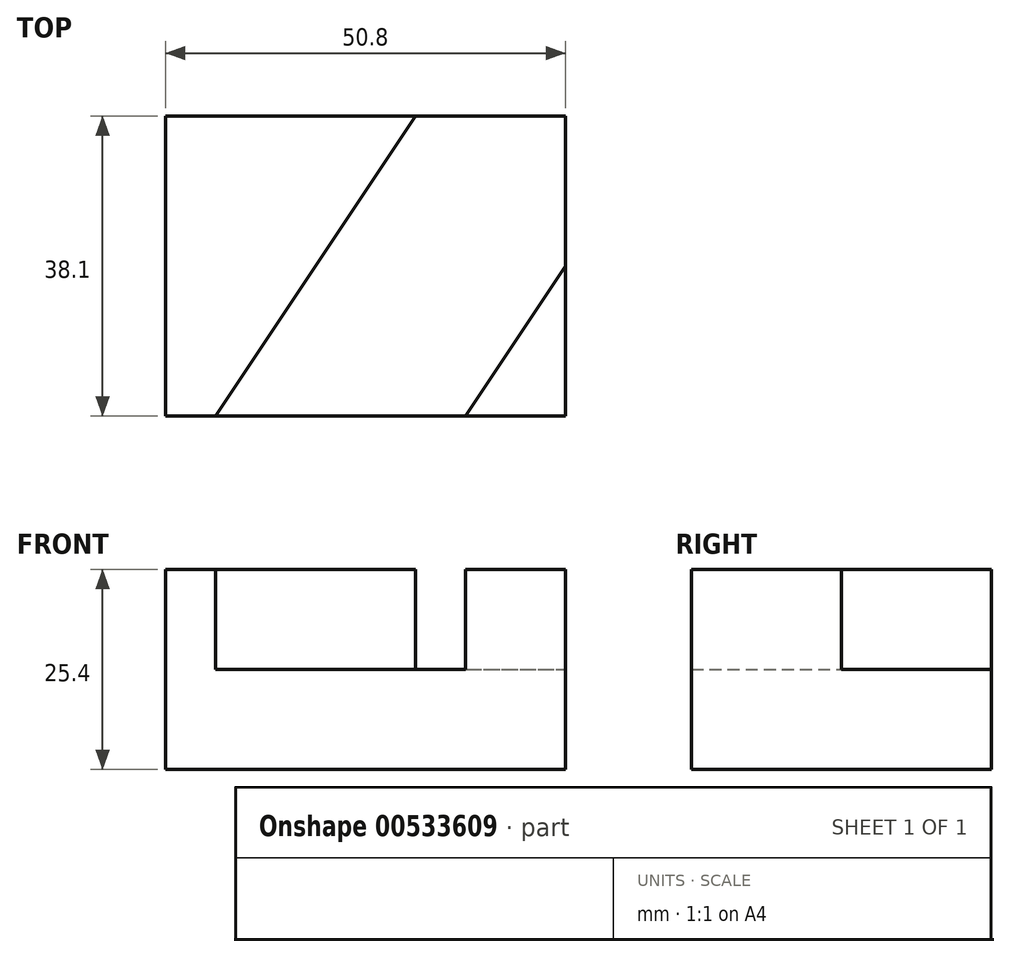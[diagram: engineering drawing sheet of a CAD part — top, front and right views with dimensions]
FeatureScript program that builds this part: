
annotation { "Feature Type Name" : "Feature", "Feature Type Description" : "" }
export const myFeature = defineFeature(function(context is Context, id is Id, definition is map)
    precondition{}
    {
        {
            var Q0;
            Q0=qCreatedBy(makeId("Front.planeOp"),FACE);
            var sketch = newSketch(context, id + "F0", { "sketchPlane" : qUnion([Q0])});
            skLineSegment(sketch, "E0.bottom", {"start": v(-68.04, 26.34) * mm, "end": v(-17.24, 26.34) * mm});
            skLineSegment(sketch, "E0.top", {"start": v(-68.04, 13.64) * mm, "end": v(-17.24, 13.64) * mm});
            skLineSegment(sketch, "E0.left", {"start": v(-68.04, 26.34) * mm, "end": v(-68.04, 13.64) * mm});
            skLineSegment(sketch, "E0.right", {"start": v(-17.24, 26.34) * mm, "end": v(-17.24, 13.64) * mm});
            skSolve(sketch);
        }
        {
            var Q0;
            Q0=makeQuery(id+"F0.imprint","IMPRINT",FACE,{"disambiguationData":[TD([[makeQuery(id+"F0.imprint","IMPRINT",EDGE,{"derivedFrom":sQuery(id+"F0.wireOp",EDGE,"E0.bottom")}),-1.0]])]});
            extrude(context, id + "F1", {"entities" : qUnion([Q0]), "depth" : 38.1 * mm, "offsetDistance" : 25.4 * mm});
        }
        {
            var Q0;
            Q0=makeQuery(id+"F1.opExtrude","SWEPT_FACE",FACE,{"disambiguationData":[OSD([sQuery(id+"F0.wireOp",EDGE,"E0.bottom")])]});
            var sketch = newSketch(context, id + "F2", { "sketchPlane" : qUnion([Q0])});
            skLineSegment(sketch, "E1", {"start": v(-29.94, -38.1) * mm, "end": v(-17.24, -19.05) * mm});
            skSolve(sketch);
        }
        {
            var Q0;
            Q0 = qSketchRegion(id + "F2", true);
            var Q1;
            {var subQ0=sQuery(id+"F2.wireOp",EDGE,"E1");Q1=makeQuery(id+"F2.imprint","IMPRINT",FACE,{"disambiguationData":[TD([[makeQuery(id+"F2.imprint","IMPRINT",EDGE,{"derivedFrom":subQ0}),-1.0]])]});}
            extrude(context, id + "F3", {"entities" : qUnion([Q0, Q1]), "operationType" : NewBodyOperationType.ADD, "depth" : 12.7 * mm, "offsetDistance" : 25.4 * mm});
        }
        {
            var Q0;
            Q0=makeQuery(id+"F1.opExtrude","SWEPT_FACE",FACE,{"disambiguationData":[OSD([sQuery(id+"F0.wireOp",EDGE,"E0.bottom")])]});
            var sketch = newSketch(context, id + "F4", { "sketchPlane" : qUnion([Q0])});
            skLineSegment(sketch, "E2", {"start": v(-68.04, -38.1) * mm, "end": v(-61.7, -38.1) * mm});
            skLineSegment(sketch, "E3", {"start": v(-61.7, -38.1) * mm, "end": v(-36.3, 0) * mm});
            skLineSegment(sketch, "E4", {"start": v(-36.3, 0) * mm, "end": v(-68.04, 0) * mm});
            skLineSegment(sketch, "E5", {"start": v(-68.04, 0) * mm, "end": v(-68.04, -38.1) * mm});
            skSolve(sketch);
        }
        {
            var Q0;
            Q0=makeQuery(id+"F4.imprint","IMPRINT",FACE,{"disambiguationData":[TD([[makeQuery(id+"F4.imprint","IMPRINT",EDGE,{"derivedFrom":sQuery(id+"F4.wireOp",EDGE,"E2")}),1.0]])]});
            extrude(context, id + "F5", {"entities" : qUnion([Q0]), "operationType" : NewBodyOperationType.ADD, "depth" : 12.7 * mm, "offsetDistance" : 25.4 * mm});
        }
    });
